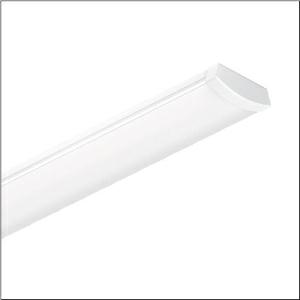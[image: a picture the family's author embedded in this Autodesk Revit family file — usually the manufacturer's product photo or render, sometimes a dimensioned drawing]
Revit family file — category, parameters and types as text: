
# Revit family: siluette_r__21_51ln12mkm40a3g_b368
name_source: partatom
category: Lighting Fixtures
units: mm (PartAtom-declared; Revit-internal decimal feet)

## family parameters
Cut with Voids When Loaded = No
Host = Face
Light Source = No
Part Type = Normal
Room Calculation Point = No
Round Connector Dimension = Use Diameter
Shared = No

## types (1)
- --- (1 x LED, 2980 lm, 20.6 W, 5000K)
    Apparent Load = 21 VA
    CIE Flux Codes = 43 73 92 94 100
    Color Rendering = 80
    Color Temperature = 5000K
    Default Elevation = 1800 mm
    Description = Siluette® 21, office luminaire, primary optical cover: enclosure, of PC, frosted, light emission: direct distribution, primary light characteristic: symmetric, installation type: suspended mounting, surface-mounted, LED, rated luminous flux: 4.800lm, luminous efficacy: 135lm/W, light colour: 830/840/850, colour temperature: 3000/4000/5000K, with terminal, 4-pole, mains connection: 220..240V, AC, 50/60Hz, rated input power: 35W, control gear: single battery element, housing, of sheet steel, white, length: 1.200mm, width: 152mm, height: 53mm, end cap, of PMMA, white, protection rating (complete): IP44, insulation class (complete): insulation class I (protective earthing), certification: CE, UKCA, protection symbol: D, permissible operating ambient temperature: -20..+40°C, standard: EN 60598-2-22, contact your sales advisor before using the luminaires in applications with unclear chemical exposure, large temperature fluctuations or condensation-forming humidity, corresponds to IFS (International Featured Standards) requirements for safety and quality in the food industry, packaging unit: 1 piece
    Height = 52 mm  [stored 0.170604 ft]
    Lamp = 1 x LED
    Lamp Light Flux = 2980 lm
    Lamp Power = 20.6 W
    Lamp count = 1
    Length = 1185 mm
    Luminous efficacy = 145 lm/W
    Manufacturer = Siteco
    ModVariant = No
    Model = 51LN12MKM40A3G
    Mounting Place = Ceiling
    Mounting Type = Pendant
    Number of Poles = 1
    OnlyDefault = Yes
    Power Factor = 1
    Product Name = Siluette® 21
    Product group = office luminaire | ceiling pendant
    ProductGroupID = 902
    Protection Class = Protection class I
    Protection Degree = IP 44
    RLX_Detail_Level = 1
    RLX_Emergency_Light_Flux = 0 lm
    RLX_Emergency_Type = 0
    RLX_Emergency_Type_DB = No
    RlxData = <blob elided: 20557 chars, md5=b1a64b17>
    Socket = socket
    Standby Power = 0 W
    System Light Flux = 2980 lm
    System Power = 21 W
    Type Comments = individual setting: colour temperature 5000K, luminous flux: 60 % | (OFF | OFF | ON) | 200 mA
    Type Image = l_1296910.jpg
    URL = http://relux.com
    VarID = @adj_001833
    Voltage = 0 V
    Weight = 0.00 kg
    Width = 152 mm

note: [stored X ft] marks values corroborated as IEEE doubles in the binary element streams (Revit-internal decimal feet)

## geometry (parser evidence)
native form markers: Blend x4, Sweep x11
no freeform markers — native parametric forms only
